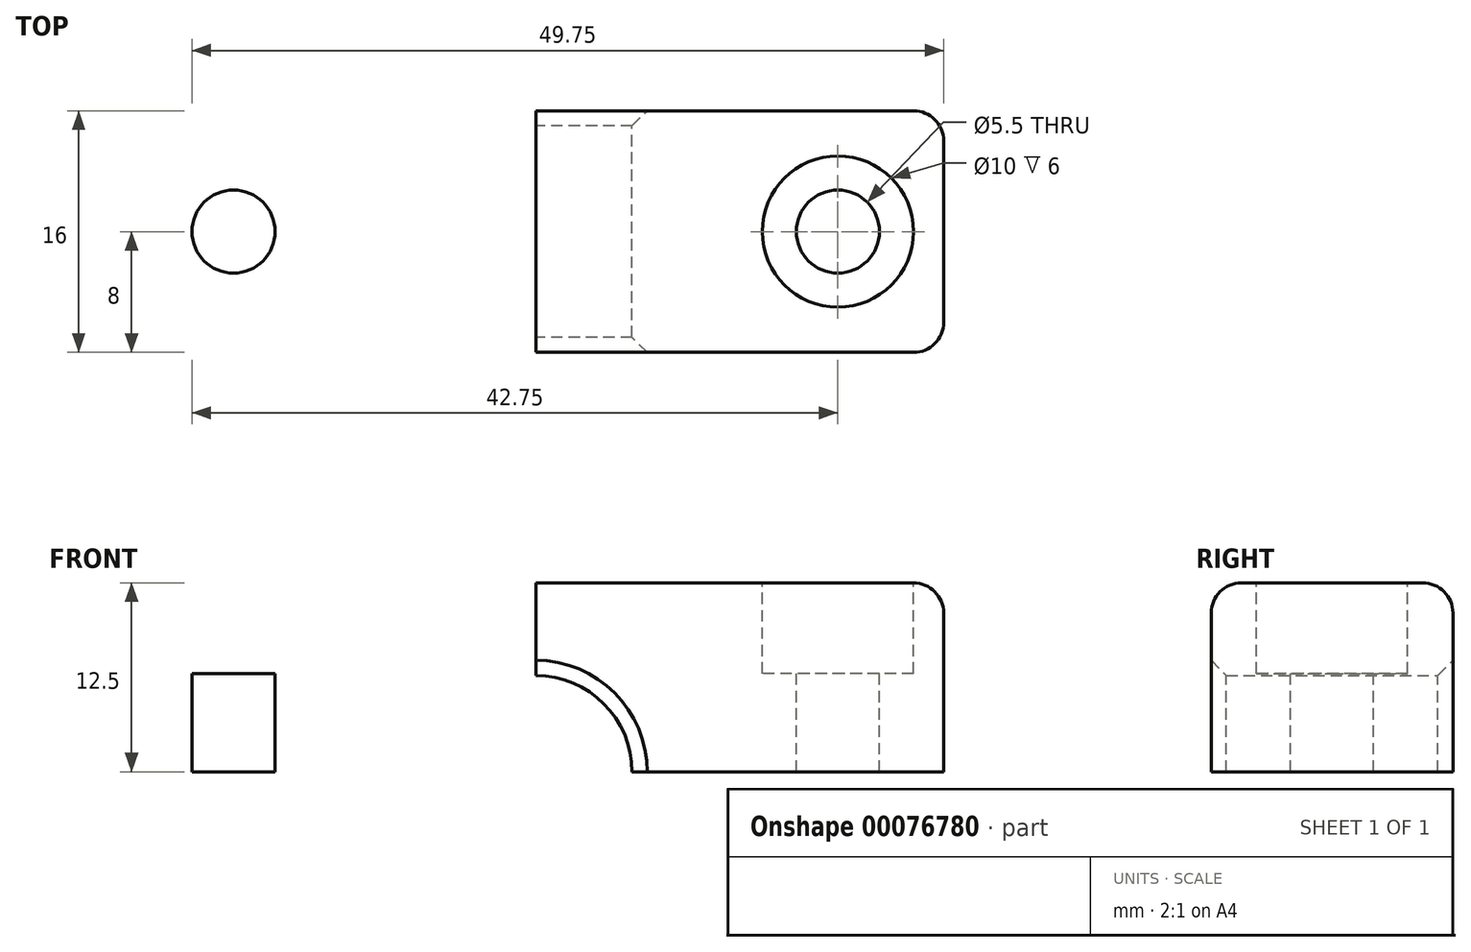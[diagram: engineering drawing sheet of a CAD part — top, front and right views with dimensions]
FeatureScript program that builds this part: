
annotation { "Feature Type Name" : "Feature", "Feature Type Description" : "" }
export const myFeature = defineFeature(function(context is Context, id is Id, definition is map)
    precondition{}
    {
        {
            var Q0;
            Q0=qCreatedBy(makeId("Front.planeOp"),FACE);
            var sketch = newSketch(context, id + "F0", { "sketchPlane" : qUnion([Q0])});
            skLineSegment(sketch, "E0.bottom", {"start": v(-27, 12.5) * mm, "end": v(27, 12.5) * mm});
            skLineSegment(sketch, "E0.top", {"start": v(-27, -12.5) * mm, "end": v(27, -12.5) * mm});
            skLineSegment(sketch, "E0.left", {"start": v(-27, 12.5) * mm, "end": v(-27, -12.5) * mm});
            skLineSegment(sketch, "E0.right", {"start": v(27, 12.5) * mm, "end": v(27, -12.5) * mm});
            skLineSegment(sketch, "E1", {"start": v(-27, 0) * mm, "end": v(27, 0) * mm});
            skPoint(sketch, "E2", {"position": v(0, 0) * mm});
            skCircle(sketch, "E3", {"center": v(0, 0) * mm, "radius": 6.38 * mm});
            skSolve(sketch);
        }
        {
            var Q0;
            {var subQ6=sQuery(id+"F0.wireOp",EDGE,"E0.bottom");Q0=makeQuery(id+"F0.imprint","IMPRINT",FACE,{"disambiguationData":[TD([[makeQuery(id+"F0.imprint","IMPRINT",EDGE,{"derivedFrom":subQ6}),-1.0]])]});}
            extrude(context, id + "F1", {"entities" : qUnion([Q0]), "depth" : 16 * mm});
        }
        {
            var Q0;
            Q0=makeQuery(id+"F1.opExtrude","SWEPT_FACE",FACE,{"disambiguationData":[OSD([sQuery(id+"F0.wireOp",EDGE,"E0.bottom")])]});
            var sketch = newSketch(context, id + "F2", { "sketchPlane" : qUnion([Q0])});
            skLineSegment(sketch, "E4", {"start": v(-27, -8) * mm, "end": v(27, -8) * mm});
            skCircle(sketch, "E5", {"center": v(-20, -8) * mm, "radius": 2.75 * mm});
            skLineSegment(sketch, "E6", {"start": v(0, 0) * mm, "end": v(0, -16) * mm});
            skCircle(sketch, "E7.MirrorC", {"center": v(20, -8) * mm, "radius": 2.75 * mm});
            skSolve(sketch);
        }
        {
            var Q0;
            {var subQ0=sQuery(id+"F2.wireOp",EDGE,"E5");var subQ1=sQuery(id+"F2.wireOp",EDGE,"E4");var subQ2=makeQuery(id+"F2.imprint","INTERSECT",VERTEX,{"disambiguationData":[OD(0.0)],"derivedFrom":[subQ1,subQ0]});Q0=makeQuery(id+"F2.imprint","IMPRINT",FACE,{"disambiguationData":[TD([[makeQuery(id+"F2.imprint","IMPRINT",EDGE,{"disambiguationData":[TD([[subQ2,-1.0]])],"derivedFrom":subQ1}),1.0]])]});}
            var Q1;
            {var subQ0=sQuery(id+"F2.wireOp",EDGE,"E5");var subQ1=sQuery(id+"F2.wireOp",EDGE,"E4");var subQ2=makeQuery(id+"F2.imprint","INTERSECT",VERTEX,{"disambiguationData":[OD(0.0)],"derivedFrom":[subQ1,subQ0]});Q1=makeQuery(id+"F2.imprint","IMPRINT",FACE,{"disambiguationData":[TD([[makeQuery(id+"F2.imprint","IMPRINT",EDGE,{"disambiguationData":[TD([[subQ2,-1.0]])],"derivedFrom":subQ1}),-1.0]])]});}
            var Q2;
            {var subQ0=sQuery(id+"F2.wireOp",EDGE,"E7.MirrorC");var subQ1=sQuery(id+"F2.wireOp",EDGE,"E4");var subQ2=makeQuery(id+"F2.imprint","INTERSECT",VERTEX,{"disambiguationData":[OD(0.0)],"derivedFrom":[subQ1,subQ0]});Q2=makeQuery(id+"F2.imprint","IMPRINT",FACE,{"disambiguationData":[TD([[makeQuery(id+"F2.imprint","IMPRINT",EDGE,{"disambiguationData":[TD([[subQ2,-1.0]])],"derivedFrom":subQ1}),1.0]])]});}
            var Q3;
            {var subQ0=sQuery(id+"F2.wireOp",EDGE,"E7.MirrorC");var subQ1=sQuery(id+"F2.wireOp",EDGE,"E4");var subQ2=makeQuery(id+"F2.imprint","INTERSECT",VERTEX,{"disambiguationData":[OD(0.0)],"derivedFrom":[subQ1,subQ0]});Q3=makeQuery(id+"F2.imprint","IMPRINT",FACE,{"disambiguationData":[TD([[makeQuery(id+"F2.imprint","IMPRINT",EDGE,{"disambiguationData":[TD([[subQ2,-1.0]])],"derivedFrom":subQ1}),-1.0]])]});}
            extrude(context, id + "F3", {"entities" : qUnion([Q0, Q1, Q2, Q3]), "operationType" : NewBodyOperationType.REMOVE, "endBound" : BoundingType.THROUGH_ALL, "oppositeDirection" : true, "depth" : 25 * mm});
        }
        {
            var Q0;
            Q0=makeQuery(id+"F1.opExtrude","SWEPT_FACE",FACE,{"disambiguationData":[OSD([sQuery(id+"F0.wireOp",EDGE,"E0.bottom")])]});
            var sketch = newSketch(context, id + "F4", { "sketchPlane" : qUnion([Q0])});
            skCircle(sketch, "E8", {"center": v(-20, -8) * mm, "radius": 5 * mm});
            skCircle(sketch, "E9", {"center": v(20, -8) * mm, "radius": 5 * mm});
            skSolve(sketch);
        }
        {
            var Q0;
            Q0=makeQuery(id+"F4.imprint","IMPRINT",FACE,{"disambiguationData":[TD([[makeQuery(id+"F4.imprint","IMPRINT",EDGE,{"derivedFrom":sQuery(id+"F4.wireOp",EDGE,"E8")}),1.0]])]});
            var Q1;
            Q1=makeQuery(id+"F4.imprint","IMPRINT",FACE,{"disambiguationData":[TD([[makeQuery(id+"F4.imprint","IMPRINT",EDGE,{"derivedFrom":sQuery(id+"F4.wireOp",EDGE,"E9")}),1.0]])]});
            extrude(context, id + "F5", {"entities" : qUnion([Q0, Q1]), "operationType" : NewBodyOperationType.REMOVE, "oppositeDirection" : true, "depth" : 6 * mm});
        }
        {
            var Q0;
            Q0=makeQuery(id+"F1.opExtrude","CAP_EDGE",EDGE,{"disambiguationData":[OSD([sQuery(id+"F0.wireOp",EDGE,"E3")])],"isStart":false});
            var Q1;
            Q1=makeQuery(id+"F1.opExtrude","CAP_EDGE",EDGE,{"disambiguationData":[OSD([sQuery(id+"F0.wireOp",EDGE,"E3")])],"isStart":true});
            chamfer(context, id + "F6", {"entities" : qUnion([Q0, Q1]), "width" : 1 * mm, "tangentPropagation" : true});
        }
        {
            var Q0;
            Q0=makeQuery(id+"F1.opExtrude","CAP_EDGE",EDGE,{"disambiguationData":[OSD([sQuery(id+"F0.wireOp",EDGE,"E0.right")])],"isStart":true});
            var Q1;
            Q1=makeQuery(id+"F1.opExtrude","CAP_EDGE",EDGE,{"disambiguationData":[OSD([sQuery(id+"F0.wireOp",EDGE,"E0.right")])],"isStart":false});
            var Q2;
            Q2=makeQuery(id+"F1.opExtrude","CAP_EDGE",EDGE,{"disambiguationData":[OSD([sQuery(id+"F0.wireOp",EDGE,"E0.left")])],"isStart":true});
            var Q3;
            Q3=makeQuery(id+"F1.opExtrude","CAP_EDGE",EDGE,{"disambiguationData":[OSD([sQuery(id+"F0.wireOp",EDGE,"E0.left")])],"isStart":false});
            fillet(context, id + "F7", {"entities" : qUnion([Q0, Q1, Q2, Q3]), "radius" : 2 * mm, "tangentPropagation" : true, "allowEdgeOverflow" : false});
        }
        {
            var Q0;
            Q0=makeQuery(id+"F1.opExtrude","CAP_EDGE",EDGE,{"disambiguationData":[OSD([sQuery(id+"F0.wireOp",EDGE,"E0.bottom")])],"isStart":true});
            fillet(context, id + "F8", {"entities" : qUnion([Q0]), "radius" : 2 * mm, "tangentPropagation" : true, "allowEdgeOverflow" : false});
        }
    });
